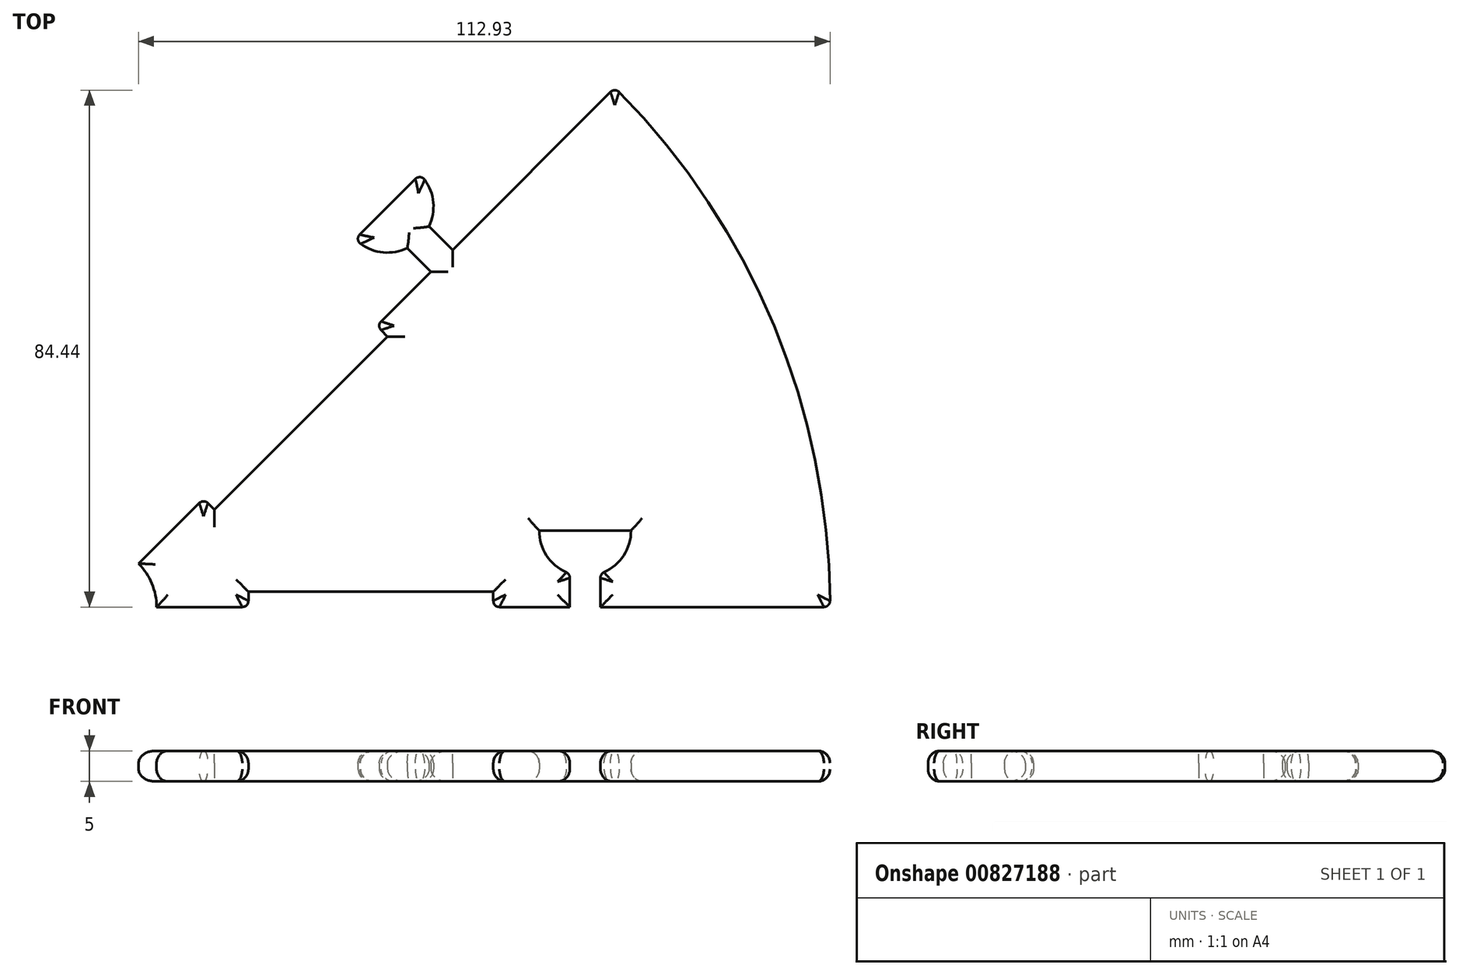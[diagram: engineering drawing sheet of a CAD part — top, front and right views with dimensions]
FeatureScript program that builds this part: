
annotation { "Feature Type Name" : "Feature", "Feature Type Description" : "" }
export const myFeature = defineFeature(function(context is Context, id is Id, definition is map)
    precondition{}
    {
        {
            var Q0;
            Q0=qCreatedBy(makeId("Top.planeOp"),FACE);
            var sketch = newSketch(context, id + "F0", { "sketchPlane" : qUnion([Q0])});
            skArc(sketch, "E0", {"start": v(120, 0) * mm, "mid": v(84.85, 84.85) * mm, "end": v(0, 120) * mm});
            skLineSegment(sketch, "E1", {"start": v(10, 0) * mm, "end": v(25, 0) * mm});
            skLineSegment(sketch, "E2", {"start": v(0, 10) * mm, "end": v(0, 120) * mm});
            skLineSegment(sketch, "E3", {"start": v(7.07, 7.07) * mm, "end": v(17.68, 17.68) * mm});
            skPoint(sketch, "E4.start.orphan", {"position": v(53.03, 81.32) * mm});
            skPoint(sketch, "E5.end.orphan", {"position": v(53.03, 60.1) * mm});
            skPoint(sketch, "E5.start.orphan", {"position": v(56.57, 56.57) * mm});
            skPoint(sketch, "E6.start.orphan", {"position": v(31.82, 60.1) * mm});
            skArc(sketch, "E7", {"start": v(54.5, 62.18) * mm, "mid": v(55.12, 66.68) * mm, "end": v(53.03, 70.71) * mm});
            skLineSegment(sketch, "E8", {"start": v(50.96, 58.64) * mm, "end": v(54.8, 54.8) * mm});
            skLineSegment(sketch, "E9", {"start": v(54.5, 62.18) * mm, "end": v(58.34, 58.34) * mm});
            skLineSegment(sketch, "E10.trimOffspring", {"start": v(58.34, 58.34) * mm, "end": v(84.85, 84.85) * mm});
            skLineSegment(sketch, "E11", {"start": v(47.73, 65.4) * mm, "end": v(50.03, 67.7) * mm});
            skLineSegment(sketch, "E12", {"start": v(47.73, 65.4) * mm, "end": v(45.28, 62.96) * mm});
            skLineSegment(sketch, "E13", {"start": v(50.03, 67.7) * mm, "end": v(53.03, 70.71) * mm});
            skLineSegment(sketch, "E14", {"start": v(45.28, 62.96) * mm, "end": v(42.43, 60.1) * mm});
            skArc(sketch, "E15.trimOffspring", {"start": v(42.43, 60.1) * mm, "mid": v(46.46, 58.02) * mm, "end": v(50.96, 58.64) * mm});
            skLineSegment(sketch, "E16.1.1", {"start": v(82.5, 5.43) * mm, "end": v(82.5, 0) * mm});
            skArc(sketch, "E16.1.2", {"start": v(82.5, 5.43) * mm, "mid": v(86.12, 8.17) * mm, "end": v(87.5, 12.5) * mm});
            skLineSegment(sketch, "E16.1.3", {"start": v(83.25, 12.5) * mm, "end": v(87.5, 12.5) * mm});
            skLineSegment(sketch, "E16.1.4", {"start": v(80, 12.5) * mm, "end": v(83.25, 12.5) * mm});
            skLineSegment(sketch, "E16.1.5", {"start": v(80, 12.5) * mm, "end": v(76.53, 12.5) * mm});
            skLineSegment(sketch, "E16.1.6", {"start": v(76.53, 12.5) * mm, "end": v(72.5, 12.5) * mm});
            skArc(sketch, "E16.1.7", {"start": v(72.5, 12.5) * mm, "mid": v(73.88, 8.17) * mm, "end": v(77.5, 5.43) * mm});
            skLineSegment(sketch, "E16.1.8", {"start": v(77.5, 5.43) * mm, "end": v(77.5, 0) * mm});
            skLineSegment(sketch, "E16.anchor1", {"start": v(0, 10) * mm, "end": v(0, 120) * mm, "construction": true});
            skLineSegment(sketch, "E16.anchor2", {"start": v(10, 0) * mm, "end": v(25, 0) * mm, "construction": true});
            skLineSegment(sketch, "E17.trimOffspring", {"start": v(82.5, 0) * mm, "end": v(120, 0) * mm, "construction": true});
            skLineSegment(sketch, "E18.trimOffspring", {"start": v(82.5, 0) * mm, "end": v(120, 0) * mm});
            skLineSegment(sketch, "E19", {"start": v(17.68, 17.68) * mm, "end": v(15.9, 19.45) * mm});
            skLineSegment(sketch, "E20", {"start": v(15.9, 19.45) * mm, "end": v(44.2, 47.73) * mm});
            skLineSegment(sketch, "E21", {"start": v(44.2, 47.73) * mm, "end": v(45.96, 45.96) * mm});
            skLineSegment(sketch, "E22.trimOffspring", {"start": v(45.96, 45.96) * mm, "end": v(54.8, 54.8) * mm});
            skLineSegment(sketch, "E23.MirrorCS", {"start": v(47.73, 44.2) * mm, "end": v(45.96, 45.96) * mm});
            skLineSegment(sketch, "E24.MirrorCS", {"start": v(19.45, 15.9) * mm, "end": v(47.73, 44.2) * mm});
            skLineSegment(sketch, "E25.MirrorCS", {"start": v(17.68, 17.68) * mm, "end": v(19.45, 15.9) * mm});
            skLineSegment(sketch, "E26.1.3", {"start": v(65, 2.5) * mm, "end": v(65, 0) * mm});
            skLineSegment(sketch, "E26.1.4", {"start": v(25, 2.5) * mm, "end": v(65, 2.5) * mm});
            skLineSegment(sketch, "E26.1.6", {"start": v(25, 0) * mm, "end": v(25, 2.5) * mm});
            skLineSegment(sketch, "E27.trimOffspring", {"start": v(65, 0) * mm, "end": v(77.5, 0) * mm, "construction": true});
            skLineSegment(sketch, "E28.trimOffspring", {"start": v(65, 0) * mm, "end": v(77.5, 0) * mm});
            skArc(sketch, "E29", {"start": v(10, 0) * mm, "mid": v(7.07, 7.07) * mm, "end": v(0, 10) * mm});
            skSolve(sketch);
        }
        {
            var Q0;
            Q0=makeQuery(id+"F0.imprint","IMPRINT",FACE,{"disambiguationData":[TD([[makeQuery(id+"F0.imprint","IMPRINT",EDGE,{"derivedFrom":sQuery(id+"F0.wireOp",EDGE,"E7")}),1.0]])]});
            extrude(context, id + "F1", {"entities" : qUnion([Q0]), "depth" : 5 * mm, "offsetDistance" : 25 * mm});
        }
        {
            var Q0;
            Q0=makeQuery(id+"F1.opExtrude","CAP_FACE",FACE,{"disambiguationData":[OSD([sQuery(id+"F0.wireOp",EDGE,"E0"),sQuery(id+"F0.wireOp",EDGE,"E3"),sQuery(id+"F0.wireOp",EDGE,"E7"),sQuery(id+"F0.wireOp",EDGE,"E8"),sQuery(id+"F0.wireOp",EDGE,"E9"),sQuery(id+"F0.wireOp",EDGE,"E11"),sQuery(id+"F0.wireOp",EDGE,"E12"),sQuery(id+"F0.wireOp",EDGE,"E13"),sQuery(id+"F0.wireOp",EDGE,"E14"),sQuery(id+"F0.wireOp",EDGE,"E15.trimOffspring"),sQuery(id+"F0.wireOp",EDGE,"E16.1.1"),sQuery(id+"F0.wireOp",EDGE,"E16.1.2"),sQuery(id+"F0.wireOp",EDGE,"E16.1.3"),sQuery(id+"F0.wireOp",EDGE,"E16.1.4"),sQuery(id+"F0.wireOp",EDGE,"E16.1.5"),sQuery(id+"F0.wireOp",EDGE,"E16.1.6"),sQuery(id+"F0.wireOp",EDGE,"E16.1.7"),sQuery(id+"F0.wireOp",EDGE,"E16.1.8"),sQuery(id+"F0.wireOp",EDGE,"E1"),sQuery(id+"F0.wireOp",EDGE,"E18.trimOffspring"),sQuery(id+"F0.wireOp",EDGE,"E10.trimOffspring"),sQuery(id+"F0.wireOp",EDGE,"E22.trimOffspring"),sQuery(id+"F0.wireOp",EDGE,"E23.MirrorCS"),sQuery(id+"F0.wireOp",EDGE,"E24.MirrorCS"),sQuery(id+"F0.wireOp",EDGE,"E25.MirrorCS"),sQuery(id+"F0.wireOp",EDGE,"E26.1.3"),sQuery(id+"F0.wireOp",EDGE,"E26.1.4"),sQuery(id+"F0.wireOp",EDGE,"E26.1.6"),sQuery(id+"F0.wireOp",EDGE,"E28.trimOffspring"),sQuery(id+"F0.wireOp",EDGE,"E29")])],"isStart":false});
            var Q1;
            Q1=makeQuery(id+"F1.opExtrude","CAP_FACE",FACE,{"disambiguationData":[OSD([sQuery(id+"F0.wireOp",EDGE,"E0"),sQuery(id+"F0.wireOp",EDGE,"E3"),sQuery(id+"F0.wireOp",EDGE,"E7"),sQuery(id+"F0.wireOp",EDGE,"E8"),sQuery(id+"F0.wireOp",EDGE,"E9"),sQuery(id+"F0.wireOp",EDGE,"E11"),sQuery(id+"F0.wireOp",EDGE,"E12"),sQuery(id+"F0.wireOp",EDGE,"E13"),sQuery(id+"F0.wireOp",EDGE,"E14"),sQuery(id+"F0.wireOp",EDGE,"E15.trimOffspring"),sQuery(id+"F0.wireOp",EDGE,"E16.1.1"),sQuery(id+"F0.wireOp",EDGE,"E16.1.2"),sQuery(id+"F0.wireOp",EDGE,"E16.1.3"),sQuery(id+"F0.wireOp",EDGE,"E16.1.4"),sQuery(id+"F0.wireOp",EDGE,"E16.1.5"),sQuery(id+"F0.wireOp",EDGE,"E16.1.6"),sQuery(id+"F0.wireOp",EDGE,"E16.1.7"),sQuery(id+"F0.wireOp",EDGE,"E16.1.8"),sQuery(id+"F0.wireOp",EDGE,"E1"),sQuery(id+"F0.wireOp",EDGE,"E18.trimOffspring"),sQuery(id+"F0.wireOp",EDGE,"E10.trimOffspring"),sQuery(id+"F0.wireOp",EDGE,"E22.trimOffspring"),sQuery(id+"F0.wireOp",EDGE,"E23.MirrorCS"),sQuery(id+"F0.wireOp",EDGE,"E24.MirrorCS"),sQuery(id+"F0.wireOp",EDGE,"E25.MirrorCS"),sQuery(id+"F0.wireOp",EDGE,"E26.1.3"),sQuery(id+"F0.wireOp",EDGE,"E26.1.4"),sQuery(id+"F0.wireOp",EDGE,"E26.1.6"),sQuery(id+"F0.wireOp",EDGE,"E28.trimOffspring"),sQuery(id+"F0.wireOp",EDGE,"E29")])],"isStart":true});
            fillet(context, id + "F2", {"entities" : qUnion([Q0, Q1]), "radius" : 2 * mm, "tangentPropagation" : true, "allowEdgeOverflow" : false});
        }
        {
            var Q0;
            Q0=makeQuery(id+"F1.opExtrude","SWEPT_EDGE",EDGE,{"disambiguationData":[OSD([sQuery(id+"F0.wireOp",EDGE,"E7"),sQuery(id+"F0.wireOp",EDGE,"E13")])]});
            var Q1;
            Q1=makeQuery(id+"F1.opExtrude","SWEPT_EDGE",EDGE,{"disambiguationData":[OSD([sQuery(id+"F0.wireOp",EDGE,"E14"),sQuery(id+"F0.wireOp",EDGE,"E15.trimOffspring")])]});
            var Q2;
            Q2=makeQuery(id+"F1.opExtrude","SWEPT_EDGE",EDGE,{"disambiguationData":[OSD([sQuery(id+"F0.wireOp",EDGE,"E21"),sQuery(id+"F0.wireOp",EDGE,"E22.trimOffspring"),sQuery(id+"F0.wireOp",EDGE,"E23.MirrorCS")])]});
            var Q3;
            Q3=makeQuery(id+"F1.opExtrude","SWEPT_EDGE",EDGE,{"disambiguationData":[OSD([sQuery(id+"F0.wireOp",EDGE,"E3"),sQuery(id+"F0.wireOp",EDGE,"E19"),sQuery(id+"F0.wireOp",EDGE,"E25.MirrorCS")])]});
            var Q4;
            Q4=makeQuery(id+"F1.opExtrude","SWEPT_EDGE",EDGE,{"disambiguationData":[OSD([sQuery(id+"F0.wireOp",EDGE,"E0"),sQuery(id+"F0.wireOp",EDGE,"E10.trimOffspring")])]});
            var Q5;
            Q5=makeQuery(id+"F1.opExtrude","SWEPT_EDGE",EDGE,{"disambiguationData":[OSD([sQuery(id+"F0.wireOp",EDGE,"E0"),sQuery(id+"F0.wireOp",EDGE,"E18.trimOffspring")])]});
            var Q6;
            Q6=makeQuery(id+"F1.opExtrude","SWEPT_EDGE",EDGE,{"disambiguationData":[OSD([sQuery(id+"F0.wireOp",EDGE,"E16.1.7"),sQuery(id+"F0.wireOp",EDGE,"E16.1.8")])]});
            var Q7;
            Q7=makeQuery(id+"F1.opExtrude","SWEPT_EDGE",EDGE,{"disambiguationData":[OSD([sQuery(id+"F0.wireOp",EDGE,"E16.1.1"),sQuery(id+"F0.wireOp",EDGE,"E16.1.2")])]});
            var Q8;
            Q8=makeQuery(id+"F1.opExtrude","SWEPT_EDGE",EDGE,{"disambiguationData":[OSD([sQuery(id+"F0.wireOp",EDGE,"E26.1.3"),sQuery(id+"F0.wireOp",EDGE,"E28.trimOffspring")])]});
            var Q9;
            Q9=makeQuery(id+"F1.opExtrude","SWEPT_EDGE",EDGE,{"disambiguationData":[OSD([sQuery(id+"F0.wireOp",EDGE,"E1"),sQuery(id+"F0.wireOp",EDGE,"E26.1.6")])]});
            fillet(context, id + "F3", {"entities" : qUnion([Q0, Q1, Q2, Q3, Q4, Q5, Q6, Q7, Q8, Q9]), "radius" : 1 * mm, "tangentPropagation" : true, "allowEdgeOverflow" : false});
        }
    });
